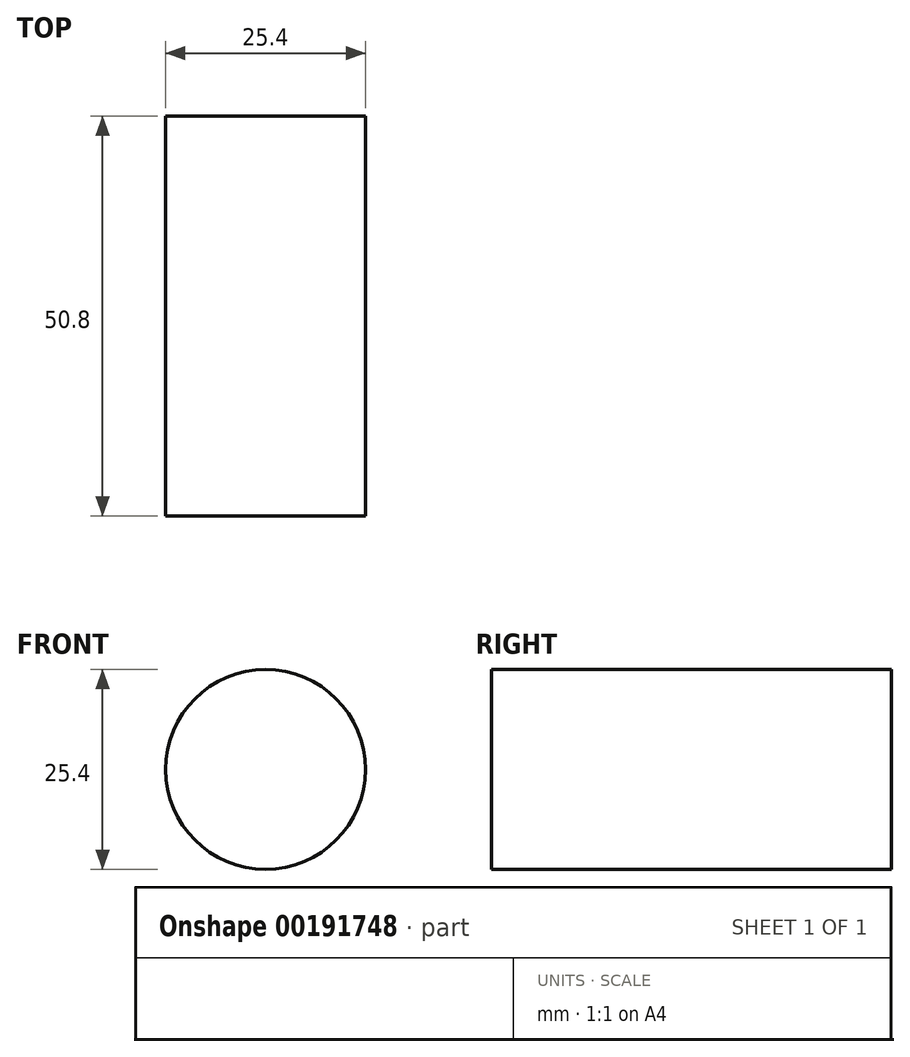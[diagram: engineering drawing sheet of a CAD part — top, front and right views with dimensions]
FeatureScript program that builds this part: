
annotation { "Feature Type Name" : "Feature", "Feature Type Description" : "" }
export const myFeature = defineFeature(function(context is Context, id is Id, definition is map)
    precondition{}
    {
        {
            var Q0;
            Q0=qCreatedBy(makeId("Front.planeOp"),FACE);
            var sketch = newSketch(context, id + "F0", { "sketchPlane" : qUnion([Q0])});
            skCircle(sketch, "E0", {"center": v(0, 0) * mm, "radius": 12.7 * mm});
            skSolve(sketch);
        }
        {
            var Q0;
            Q0 = qSketchRegion(id + "F0", true);
            extrude(context, id + "F1", {"entities" : qUnion([Q0]), "depth" : 50.8 * mm});
        }
    });
